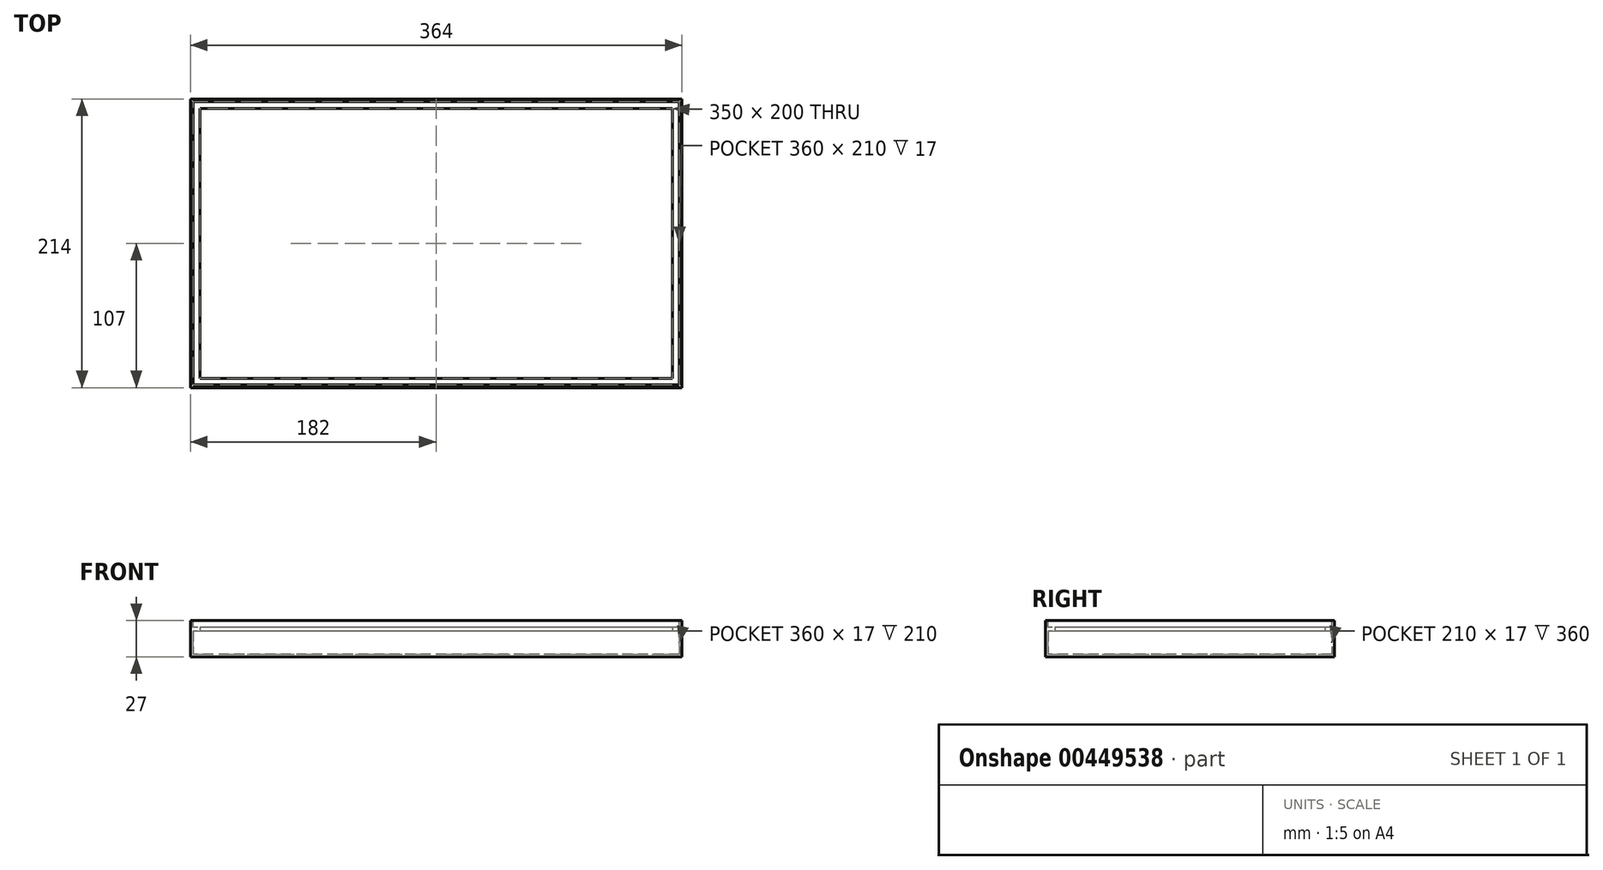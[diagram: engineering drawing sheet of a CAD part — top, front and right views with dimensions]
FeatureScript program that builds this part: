
annotation { "Feature Type Name" : "Feature", "Feature Type Description" : "" }
export const myFeature = defineFeature(function(context is Context, id is Id, definition is map)
    precondition{}
    {
        {
            var Q0;
            Q0=qCreatedBy(makeId("Top.planeOp"),FACE);
            var sketch = newSketch(context, id + "F0", { "sketchPlane" : qUnion([Q0])});
            skLineSegment(sketch, "E0.bottom", {"start": v(0, 0) * mm, "end": v(-364, 0) * mm});
            skLineSegment(sketch, "E0.top", {"start": v(0, -214) * mm, "end": v(-364, -214) * mm});
            skLineSegment(sketch, "E0.left", {"start": v(0, 0) * mm, "end": v(0, -214) * mm});
            skLineSegment(sketch, "E0.right", {"start": v(-364, 0) * mm, "end": v(-364, -214) * mm});
            skSolve(sketch);
        }
        {
            var Q0;
            Q0=makeQuery(id+"F0.imprint","IMPRINT",FACE,{"disambiguationData":[TD([[makeQuery(id+"F0.imprint","IMPRINT",EDGE,{"derivedFrom":sQuery(id+"F0.wireOp",EDGE,"E0.bottom")}),1.0]])]});
            extrude(context, id + "F1", {"entities" : qUnion([Q0]), "depth" : 27 * mm});
        }
        {
            var Q0;
            Q0=makeQuery(id+"F1.opExtrude","CAP_FACE",FACE,{"disambiguationData":[OSD([sQuery(id+"F0.wireOp",EDGE,"E0.bottom"),sQuery(id+"F0.wireOp",EDGE,"E0.top"),sQuery(id+"F0.wireOp",EDGE,"E0.left"),sQuery(id+"F0.wireOp",EDGE,"E0.right")])],"isStart":false});
            var sketch = newSketch(context, id + "F2", { "sketchPlane" : qUnion([Q0])});
            skLineSegment(sketch, "E1", {"start": v(0, 0) * mm, "end": v(-364, 0) * mm});
            skLineSegment(sketch, "E2", {"start": v(-364, 0) * mm, "end": v(-364, -214) * mm});
            skLineSegment(sketch, "E3", {"start": v(-364, -214) * mm, "end": v(0, -214) * mm});
            skLineSegment(sketch, "E4", {"start": v(0, -214) * mm, "end": v(0, 0) * mm});
            skLineSegment(sketch, "E5.bottom", {"start": v(-2, -2) * mm, "end": v(-362, -2) * mm});
            skLineSegment(sketch, "E5.top", {"start": v(-2, -212) * mm, "end": v(-362, -212) * mm});
            skLineSegment(sketch, "E5.left", {"start": v(-2, -2) * mm, "end": v(-2, -212) * mm});
            skLineSegment(sketch, "E5.right", {"start": v(-362, -2) * mm, "end": v(-362, -212) * mm});
            skPoint(sketch, "E5.middle", {"position": v(-182, -107) * mm});
            skLineSegment(sketch, "E6", {"start": v(-246.6, 0) * mm, "end": v(-246.6, -2) * mm});
            skLineSegment(sketch, "E7", {"start": v(-247.7, -214) * mm, "end": v(-247.7, -212) * mm});
            skLineSegment(sketch, "E8", {"start": v(-364, -107) * mm, "end": v(-362, -107) * mm});
            skLineSegment(sketch, "E9", {"start": v(0, -112.87) * mm, "end": v(-2, -112.87) * mm});
            skSolve(sketch);
        }
        {
            var Q0;
            {var subQ4=sQuery(id+"F2.wireOp",EDGE,"E5.left");var subQ6=sQuery(id+"F2.wireOp",EDGE,"E5.bottom");var subQ9=makeQuery(id+"F2.imprint","INTERSECT",VERTEX,{"derivedFrom":[subQ6,subQ4]});Q0=makeQuery(id+"F2.imprint","IMPRINT",FACE,{"disambiguationData":[TD([[makeQuery(id+"F2.imprint","IMPRINT",EDGE,{"disambiguationData":[TD([[subQ9,-1.0]])],"derivedFrom":subQ6}),1.0]])]});}
            extrude(context, id + "F3", {"entities" : qUnion([Q0]), "operationType" : NewBodyOperationType.REMOVE, "oppositeDirection" : true, "depth" : 25 * mm});
        }
        {
            var Q0;
            Q0=makeQuery(id+"F3.boolean.opBoolean","COPY",FACE,{"derivedFrom":makeQuery(id+"F3.opExtrude","CAP_FACE",FACE,{"disambiguationData":[OSD([sQuery(id+"F2.wireOp",EDGE,"E5.bottom"),sQuery(id+"F2.wireOp",EDGE,"E5.top"),sQuery(id+"F2.wireOp",EDGE,"E5.left"),sQuery(id+"F2.wireOp",EDGE,"E5.right")])],"isStart":false})});
            var sketch = newSketch(context, id + "F4", { "sketchPlane" : qUnion([Q0])});
            skLineSegment(sketch, "E10", {"start": v(-357, -107) * mm, "end": v(-357, -7) * mm});
            skLineSegment(sketch, "E11", {"start": v(-357, -107) * mm, "end": v(-357, -207) * mm});
            skLineSegment(sketch, "E12", {"start": v(-279.82, -207) * mm, "end": v(-357, -207) * mm});
            skLineSegment(sketch, "E13", {"start": v(-279.82, -207) * mm, "end": v(-7, -207) * mm});
            skLineSegment(sketch, "E14", {"start": v(-7, -107) * mm, "end": v(-7, -207) * mm});
            skLineSegment(sketch, "E15", {"start": v(-7, -107) * mm, "end": v(-7, -7) * mm});
            skLineSegment(sketch, "E16", {"start": v(-279.82, -7) * mm, "end": v(-7, -7) * mm});
            skLineSegment(sketch, "E17", {"start": v(-279.82, -7) * mm, "end": v(-357, -7) * mm});
            skLineSegment(sketch, "E18.bottom", {"start": v(-362, -2) * mm, "end": v(-2, -2) * mm});
            skLineSegment(sketch, "E18.top", {"start": v(-362, -212) * mm, "end": v(-2, -212) * mm});
            skLineSegment(sketch, "E18.left", {"start": v(-362, -2) * mm, "end": v(-362, -212) * mm});
            skLineSegment(sketch, "E18.right", {"start": v(-2, -2) * mm, "end": v(-2, -212) * mm});
            skPoint(sketch, "E19.start.orphan", {"position": v(-362, -107) * mm});
            skPoint(sketch, "E20.start.orphan", {"position": v(-279.82, -212) * mm});
            skPoint(sketch, "E21.start.orphan", {"position": v(-2, -107) * mm});
            skSolve(sketch);
        }
        {
            var Q0;
            Q0=makeQuery(id+"F4.imprint","IMPRINT",FACE,{"disambiguationData":[TD([[makeQuery(id+"F4.imprint","IMPRINT",EDGE,{"derivedFrom":sQuery(id+"F4.wireOp",EDGE,"E10")}),1.0]])]});
            extrude(context, id + "F5", {"entities" : qUnion([Q0]), "operationType" : NewBodyOperationType.ADD, "depth" : 20 * mm});
        }
        {
            var Q0;
            Q0 = qSketchRegion(id + "F4", true);
            extrude(context, id + "F6", {"entities" : qUnion([Q0]), "operationType" : NewBodyOperationType.REMOVE, "depth" : 17 * mm});
        }
    });
